# Revit family: ShowerCornerSpongeBasket-Double-Vitra-BaseSeries-A44158
name_source: partatom
category: Plumbing Fixtures
revit_build: Autodesk Revit 2017 (Build: 20160225_1515(x64)
units: mm (PartAtom-declared; Revit-internal decimal feet)

## family parameters
Cut with Voids When Loaded = No
Host = Face
OmniClass Number = 23.45.00.00
OmniClass Title = Sanitary, Laundry, and Cleaning Equipment
Part Type = Normal
Room Calculation Point = No
Round Connector Dimension = Use Diameter
Shared = Yes

## types (1)
- ShowerCornerSpongeBasket-Double-Vitra-BaseSeries-A44158
    Article No. (default) = A44158
    BIMobject category = Sanitary - Bathroom Accessories
    Brand = VitrA
    CW Connection = No
    Coating Material = Chrome
    Color = Chrome
    Default Elevation = 0 mm  [stored 0 ft]
    Description = Base Corner Unit - Sponge Basket
    Design country = Turkey
    HW Connection = No
    IFC Classification = Sanitary Terminal
    Main Material = Metal
    Manufacturer = Vitra
    Manufacturer name = Vitra
    Masterformat 2014 Code = 01 52 19
    Masterformat 2014 Description = Sanitary Facilities
    Model = A44158
    Mounting type = Wall Mounted
    NBS Referans Code = 31-75
    NBS Referans Description = Sanitary Accessories
    Nominal Depth (mm) = 195 mm
    Nominal Height (mm) = 340 mm
    Nominal Width (mm) = 192 mm  [stored 0.629921 ft]
    OmniClass Code = 23-19 31 17
    OmniClass Description = Sanitary Room Units
    Product SKU = A44158
    Product Type = Built-in Shower Corner Basket
    Product certification = https://www.vitraglobal.com
    Product family = BaseSeries
    Product group = Shower Corner Basket
    Product url = https://vitraglobal.com
    Technical description = https://vitraglobal.com
    UNSPSC Code = 301815
    URL = https://vitraglobal.com
    Uniclass 1.4 Code = L721
    Uniclass 1.4 Description = Sanitary equipment
    Uniclass 2.0 Code = PR-31-75
    Uniclass 2.0 Description = Sanitary Accessories
    Uniclass 2015 Code = Pr_40_20
    Uniclass 2015 Name = Sanitary fittings and accessories
    Uniformat II Code = E1090
    Uniformat II Description = Other Equipment
    Vent Connection = No
    Warranty Period (Year) = 5 years
    Waste Connection = No
    Weight Net (kg) = 2
    Youtube = https://www.youtube.com

note: [stored X ft] marks values corroborated as IEEE doubles in the binary element streams (Revit-internal decimal feet)

## geometry (parser evidence)
native form markers: Sweep x1
no freeform markers — native parametric forms only
